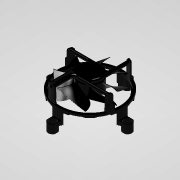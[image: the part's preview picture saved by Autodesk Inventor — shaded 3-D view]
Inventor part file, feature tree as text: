
AUTODESK INVENTOR PART (.ipt)
format: ipt  version: 2020.5 (Build 245400000, 400)  size: 1,404,416 bytes
history: native  units: in
note: dims shown in document units (in); Inventor stores cm internally (conversion verified against a paired STEP export)
features: extrude x22, sketch x19, fillet x10, plane x9, pattern_circular x4, loft x3, projected_geometry x3, mirror x2, revolve x1, split x1
ambient origin geometry x8: Origin, YZ Plane, XZ Plane, XY Plane, X Axis, Y Axis, Z Axis, Center Point
bodies: Solid1 (feature_tree), Solid2 (feature_tree)
feature tree (74):
  extrude  "Extrusion1"  Depth=0.149in
  extrude  "Extrusion2"  Depth=3.544in
  plane  "Work Plane1"
  sketch  "Sketch3"  dims[d5=0.043in d6=0.0in d7=0.585in]
  extrude  "Extrusion3"  Depth=0.585in
  extrude  "Extrusion4"  Depth=0.482in
  extrude  "Extrusion5"  Depth=0.02in
  extrude  "Extrusion6"  Depth=0.02in
  extrude  "Extrusion7"  Depth=0.505in
  fillet  "Fillet1"  Radius=0.42in
  fillet  "Fillet2"  Radius=0.223in
  extrude  "Extrusion8"  Depth=0.188in
  revolve  "Revolution1"  [1 undecoded]
  pattern_circular  "Circular Pattern1"  [2 undecoded]
  extrude  "Extrusion9"  Depth=1.05in
  fillet  "Fillet3"  Radius=0.05in
  plane  "Work Plane2"
  mirror  "Mirror1"
  sketch  "Sketch8"  dims[d14=0.38in d16=0.505in d17=0.42in d18=0.223in]
  extrude  "Extrusion10"  Depth=0.05in
  extrude  "Extrusion11"  Depth=0.1in
  fillet  "Fillet4"  Radius=0.025in
  plane  "Work Plane3"
  mirror  "Mirror2"
  plane  "Work Plane4"
  sketch  "Sketch9"  dims[d19=0.294in d20=0.188in]
  sketch  "Sketch10"  dims[d21=0.043in d22=0.0in d23=0.205in d24=0.0in]
  extrude  "Extrusion12"  Depth=0.05in
  extrude  "Extrusion13"  Depth=0.0481in
  loft  "Loft1"
  extrude  "Extrusion14"  TaperAngle=45.0deg  [1 undecoded]
  loft  "Loft2"
  plane  "Work Plane7"
  extrude  "Extrusion18"  Depth=0.53in
  sketch  "Sketch14"  dims[d33=45.0deg]
  plane  "Work Plane8"
  extrude  "Extrusion20"  Depth=0.16in
  extrude  "Extrusion21"  Depth=0.076in TaperAngle=0.0deg
  pattern_circular  "Circular Pattern2"  [2 undecoded]
  fillet  "Fillet9"  [1 undecoded]
  pattern_circular  "Circular Pattern3"  Angle=45.0deg  [1 undecoded]
  fillet  "Fillet5"  Radius=0.152in
  fillet  "Fillet6"  Radius=0.71in
  fillet  "Fillet7"  Radius=1.69in
  plane  "Work Plane5"
  sketch  "Sketch11"  dims[d25=0.279in d26=0.0in]
  plane  "Work Plane6"
  extrude  "Extrusion15"  Depth=0.076in TaperAngle=0.0deg
  extrude  "Extrusion16"  Depth=0.248in TaperAngle=0.0deg
  extrude  "Extrusion17"  Depth=0.02in
  fillet  "Fillet8"  [1 undecoded]
  split  "Split1"
  extrude  "Extrusion22"  Depth=0.854in
  extrude  "Extrusion23"  Depth=1.27in
  fillet  "Fillet10"  Radius=0.156in
  sketch  "Sketch19"  dims[d38=0.085in]
  sketch  "Sketch20"  dims[d39=0.02in]
  plane  "Work Plane9"
  loft  "Loft4"
  pattern_circular  "Circular Pattern5"  [2 undecoded]
  sketch  "Sketch1"  dims[d0=3.64in d1=0.149in]
  sketch  "Sketch2"  dims[d2=0.103in d3=0.0in d4=3.544in]
  sketch  "Sketch4"  dims[d8=0.616in d9=0.482in]
  sketch  "Sketch5"  dims[d10=0.462in d11=0.02in]
  sketch  "Sketch7"  dims[d12=0.0687in d13=0.02in]
  sketch  "Sketch12"  dims[d27=0.212in d28=0.0in]
  sketch  "Sketch13"  dims[d32=0.066in]
  sketch  "Sketch15"  dims[d34=0.1in]
  sketch  "Sketch17"  dims[d35=0.051in]
  sketch  "Sketch18"  dims[d36=0.212in d37=0.0in]
  projected_geometry  "Projected Loop2"
  projected_geometry  "Projected Loop3"
  sketch  "Sketch21"  dims[d40=2.0866in d41=1.0in d42=1.05in d43=0.05in d44=0.0in d45=0.05in d47=0.1in d48=0.025in d49=0.05in d50=0.0481in d52=1.5748in d53=360.0deg d55=45.0deg d56=0.4in d57=0.53in d58=0.16in d59=0.076in d60=0.0in d61=0.02in d62=-0.3092in d63=45.0deg d64=0.152in d65=0.71in d66=1.69in d67=0.076in d68=0.0in d69=0.248in d70=0.0in d71=0.02in d72=45.0deg d73=0.854in d74=1.27in d75=0.156in d76=0.255in d77=0.347in d78=0.424in d79=0.308in d80=0.506in d81=1.13in d82=0.18in d83=0.0in d84=0.15in d85=0.0in d86=0.0in d87=90.0deg d88=0.0in d89=90.0deg d90=0.15in d91=0.0in d92=0.0in d93=90.0deg d94=0.0in d95=90.0deg d96=1.1811in d97=180.0deg d99=0.1in d100=0.075in d101=0.06in d102=0.168in d103=0.12in d105=0.168in d106=0.3in d107=0.2in d108=0.0in d109=0.2in d110=0.0in d111=-0.02in d112=0.18in d113=0.101in d114=0.05in d115=0.05in d116=0.044in d117=0.0in d118=0.03in d119=90.0deg d120=0.05in d121=0.065in d122=0.06in d123=0.09in d124=0.013in d125=0.507in d126=0.148in d127=0.0in d128=0.467in d131=0.148in d132=0.0in d134=0.1in d135=0.033in d136=0.04in d137=0.0in d138=0.03in d139=0.7874in d140=180.0deg d142=1.05in d150=1.0in d151=0.08in d152=0.0in d153=0.66in d154=0.0in d155=0.0625in d156=0.5625in d157=2.7559in d159=360.0deg d161=1.51in d162=0.03in d163=0.1in d164=2.7559in d166=360.0deg d168=0.03in d169=0.125in d180=48.0in d181=2.0in d182=8.0in d183=0.0in d184=90.0deg d185=0.0in d186=90.0deg d187=0.0in d188=90.0deg d189=2.7559in d190=360.0deg d192=0.6in]
  projected_geometry  "Project Cut Edges1"
note: 11 required parameter values undecoded (feature->parameter linkage not recoverable at this tier; creation-order binding heuristic only, values carry confidence <= 0.55)